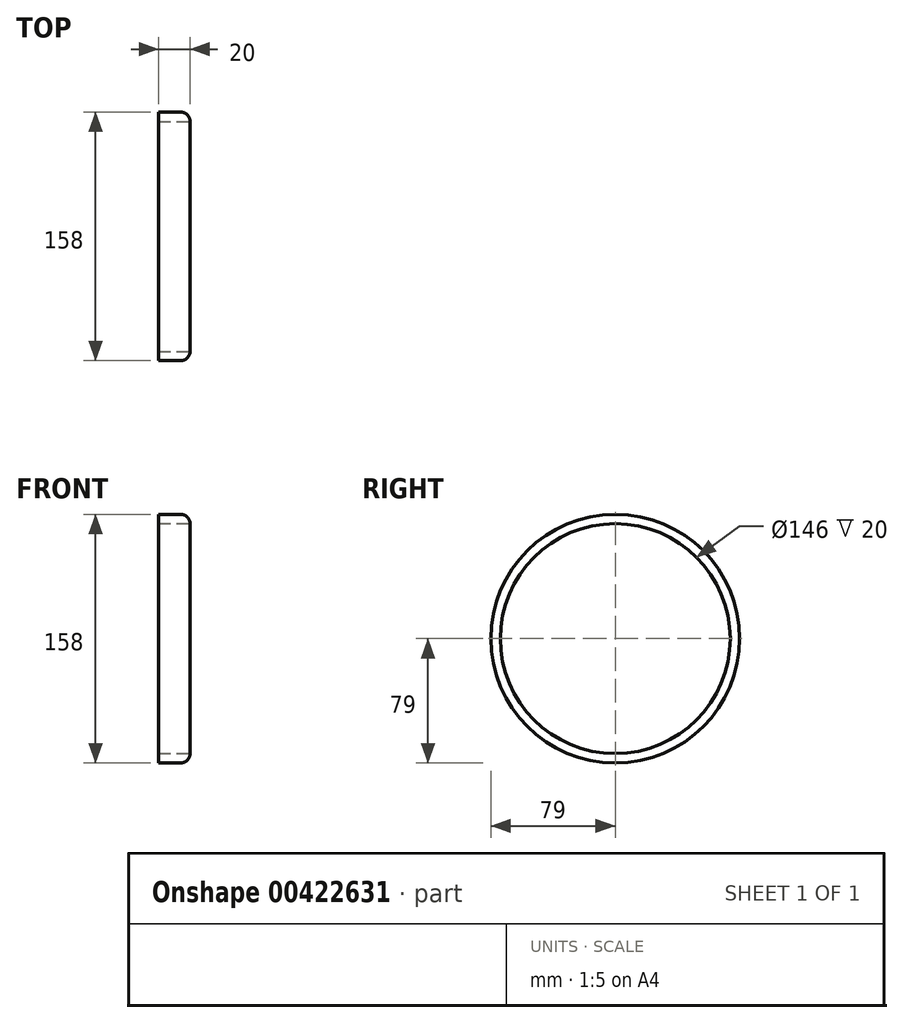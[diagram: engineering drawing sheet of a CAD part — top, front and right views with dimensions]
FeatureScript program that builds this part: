
annotation { "Feature Type Name" : "Feature", "Feature Type Description" : "" }
export const myFeature = defineFeature(function(context is Context, id is Id, definition is map)
    precondition{}
    {
        {
            var Q0;
            Q0=qCreatedBy(makeId("Right.planeOp"),FACE);
            var sketch = newSketch(context, id + "F0", { "sketchPlane" : qUnion([Q0])});
            skCircle(sketch, "E0", {"center": v(0, 0) * mm, "radius": 79 * mm});
            skSolve(sketch);
        }
        {
            var Q0;
            Q0=makeQuery(id+"F0.imprint","IMPRINT",FACE,{"disambiguationData":[TD([[makeQuery(id+"F0.imprint","IMPRINT",EDGE,{"derivedFrom":sQuery(id+"F0.wireOp",EDGE,"E0")}),1.0]])]});
            extrude(context, id + "F1", {"entities" : qUnion([Q0]), "depth" : 20 * mm});
        }
        {
            var Q0;
            Q0=makeQuery(id+"F1.opExtrude","CAP_FACE",FACE,{"disambiguationData":[OSD([sQuery(id+"F0.wireOp",EDGE,"E0")])],"isStart":false});
            fillet(context, id + "F2", {"entities" : qUnion([Q0]), "radius" : 6 * mm, "tangentPropagation" : true, "allowEdgeOverflow" : false});
        }
        {
            var Q0;
            Q0=makeQuery(id+"F1.opExtrude","CAP_FACE",FACE,{"disambiguationData":[OSD([sQuery(id+"F0.wireOp",EDGE,"E0")])],"isStart":false});
            extrude(context, id + "F3", {"entities" : qUnion([Q0]), "endBound" : BoundingType.UP_TO_NEXT, "oppositeDirection" : true, "depth" : 30 * mm});
        }
        {
            var Q0;
            Q0=makeQuery(id+"F1.opExtrude","CAP_FACE",FACE,{"disambiguationData":[OSD([sQuery(id+"F0.wireOp",EDGE,"E0")])],"isStart":false});
            extrude(context, id + "F4", {"entities" : qUnion([Q0]), "operationType" : NewBodyOperationType.REMOVE, "oppositeDirection" : true, "depth" : 25 * mm});
        }
    });
